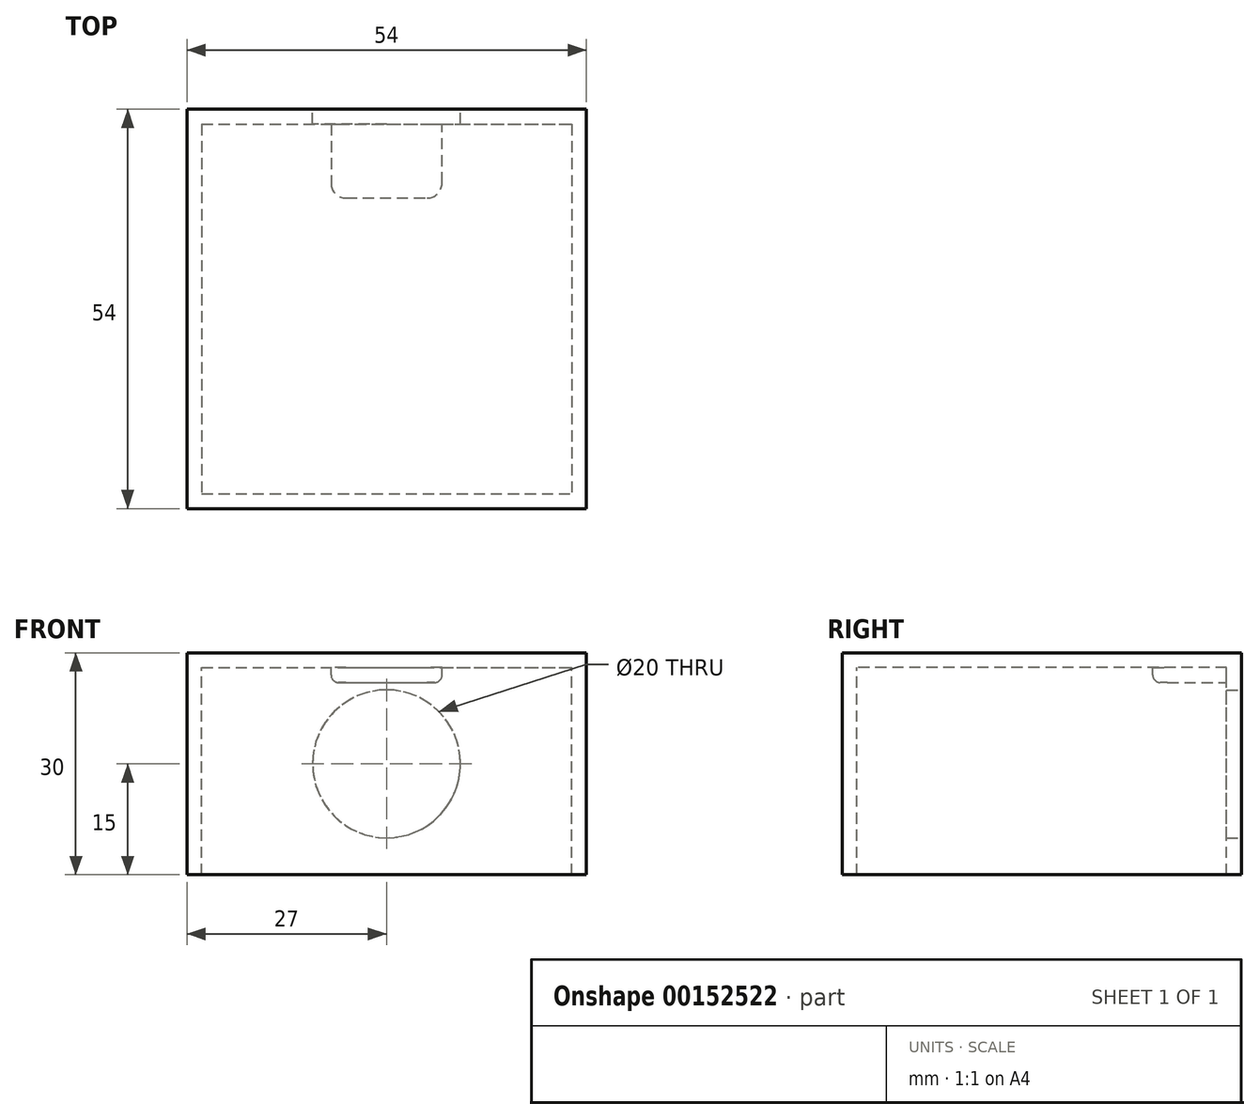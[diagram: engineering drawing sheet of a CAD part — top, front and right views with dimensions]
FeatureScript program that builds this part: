
annotation { "Feature Type Name" : "Feature", "Feature Type Description" : "" }
export const myFeature = defineFeature(function(context is Context, id is Id, definition is map)
    precondition{}
    {
        {
            var Q0;
            Q0=qCreatedBy(makeId("Top.planeOp"),FACE);
            var sketch = newSketch(context, id + "F0", { "sketchPlane" : qUnion([Q0])});
            skLineSegment(sketch, "E0.bottom", {"start": v(-27, 27) * mm, "end": v(27, 27) * mm});
            skLineSegment(sketch, "E0.top", {"start": v(-27, -27) * mm, "end": v(27, -27) * mm});
            skLineSegment(sketch, "E0.left", {"start": v(-27, 27) * mm, "end": v(-27, -27) * mm});
            skLineSegment(sketch, "E0.right", {"start": v(27, 27) * mm, "end": v(27, -27) * mm});
            skPoint(sketch, "E0.middle", {"position": v(0, 0) * mm});
            skLineSegment(sketch, "E1.bottom", {"start": v(-25, 25) * mm, "end": v(25, 25) * mm});
            skLineSegment(sketch, "E1.top", {"start": v(-25, -25) * mm, "end": v(25, -25) * mm});
            skLineSegment(sketch, "E1.left", {"start": v(-25, 25) * mm, "end": v(-25, -25) * mm});
            skLineSegment(sketch, "E1.right", {"start": v(25, 25) * mm, "end": v(25, -25) * mm});
            skSolve(sketch);
        }
        {
            var Q0;
            Q0=makeQuery(id+"F0.imprint","IMPRINT",FACE,{"disambiguationData":[TD([[makeQuery(id+"F0.imprint","IMPRINT",EDGE,{"derivedFrom":sQuery(id+"F0.wireOp",EDGE,"E1.bottom")}),-1.0]])]});
            var Q1;
            Q1=makeQuery(id+"F0.imprint","IMPRINT",FACE,{"disambiguationData":[TD([[makeQuery(id+"F0.imprint","IMPRINT",EDGE,{"derivedFrom":sQuery(id+"F0.wireOp",EDGE,"E0.bottom")}),-1.0]])]});
            extrude(context, id + "F1", {"entities" : qUnion([Q0, Q1]), "oppositeDirection" : true, "depth" : 2 * mm});
        }
        {
            var Q0;
            Q0=makeQuery(id+"F0.imprint","IMPRINT",FACE,{"disambiguationData":[TD([[makeQuery(id+"F0.imprint","IMPRINT",EDGE,{"derivedFrom":sQuery(id+"F0.wireOp",EDGE,"E0.bottom")}),-1.0]])]});
            extrude(context, id + "F2", {"entities" : qUnion([Q0]), "operationType" : NewBodyOperationType.ADD, "oppositeDirection" : true, "depth" : 30 * mm});
        }
        {
            var Q0;
            {var subQ0=sQuery(id+"F0.wireOp",EDGE,"E0.bottom");Q0=makeQuery(id+"F2.boolean.opBoolean","MERGE",FACE,{"derivedFrom":[makeQuery(id+"F1.opExtrude","SWEPT_FACE",FACE,{"disambiguationData":[OSD([subQ0])]}),makeQuery(id+"F2.opExtrude","SWEPT_FACE",FACE,{"disambiguationData":[OSD([subQ0])]})]});}
            var sketch = newSketch(context, id + "F3", { "sketchPlane" : qUnion([Q0])});
            skLineSegment(sketch, "E2.0", {"start": v(27, -30) * mm, "end": v(-27, -30) * mm});
            skLineSegment(sketch, "E3.0", {"start": v(27, 0) * mm, "end": v(-27, 0) * mm});
            skLineSegment(sketch, "E4", {"start": v(27, 0) * mm, "end": v(-27, -30) * mm, "construction": true});
            skCircle(sketch, "E5", {"center": v(0, -15) * mm, "radius": 10 * mm});
            skSolve(sketch);
        }
        {
            var Q0;
            Q0=makeQuery(id+"F3.imprint","IMPRINT",FACE,{"disambiguationData":[TD([[makeQuery(id+"F3.imprint","IMPRINT",EDGE,{"derivedFrom":sQuery(id+"F3.wireOp",EDGE,"E5")}),1.0]])]});
            extrude(context, id + "F4", {"entities" : qUnion([Q0]), "operationType" : NewBodyOperationType.REMOVE, "endBound" : BoundingType.UP_TO_NEXT, "oppositeDirection" : true, "depth" : 25 * mm});
        }
        {
            var Q0;
            Q0=makeQuery(id+"F1.opExtrude","CAP_FACE",FACE,{"disambiguationData":[OSD([sQuery(id+"F0.wireOp",EDGE,"E0.bottom"),sQuery(id+"F0.wireOp",EDGE,"E0.top"),sQuery(id+"F0.wireOp",EDGE,"E0.left"),sQuery(id+"F0.wireOp",EDGE,"E0.right")])],"isStart":false});
            var sketch = newSketch(context, id + "F5", { "sketchPlane" : qUnion([Q0])});
            skLineSegment(sketch, "E6.0", {"start": v(-25, -25) * mm, "end": v(25, -25) * mm});
            skLineSegment(sketch, "E7", {"start": v(0, 0) * mm, "end": v(0, -25) * mm, "construction": true});
            skLineSegment(sketch, "E8", {"start": v(-7.5, -25) * mm, "end": v(-7.5, -17) * mm});
            skLineSegment(sketch, "E9", {"start": v(-5.5, -15) * mm, "end": v(5.5, -15) * mm});
            skLineSegment(sketch, "E10", {"start": v(7.5, -17) * mm, "end": v(7.5, -25) * mm});
            skPoint(sketch, "E11", {"position": v(0, -15) * mm});
            skPoint(sketch, "E12.visualSharp", {"position": v(-7.5, -15) * mm});
            skArc(sketch, "E12.filletArc", {"start": v(-5.5, -15) * mm, "mid": v(-6.91, -15.59) * mm, "end": v(-7.5, -17) * mm});
            skPoint(sketch, "E13.visualSharp", {"position": v(7.5, -15) * mm});
            skArc(sketch, "E13.filletArc", {"start": v(7.5, -17) * mm, "mid": v(6.91, -15.59) * mm, "end": v(5.5, -15) * mm});
            skSolve(sketch);
        }
        {
            var Q0;
            {var subQ1=sQuery(id+"F5.wireOp",EDGE,"E8");Q0=makeQuery(id+"F5.imprint","IMPRINT",FACE,{"disambiguationData":[TD([[makeQuery(id+"F5.imprint","IMPRINT",EDGE,{"derivedFrom":subQ1}),-1.0]])]});}
            extrude(context, id + "F6", {"entities" : qUnion([Q0]), "operationType" : NewBodyOperationType.ADD, "depth" : 2 * mm});
        }
        {
            var Q0;
            Q0=makeQuery(id+"F6.opExtrude","CAP_EDGE",EDGE,{"disambiguationData":[OSD([sQuery(id+"F5.wireOp",EDGE,"E8")])],"isStart":false});
            var Q1;
            Q1=makeQuery(id+"F6.opExtrude","CAP_EDGE",EDGE,{"disambiguationData":[OSD([sQuery(id+"F5.wireOp",EDGE,"E12.filletArc")])],"isStart":false});
            var Q2;
            Q2=makeQuery(id+"F6.opExtrude","CAP_EDGE",EDGE,{"disambiguationData":[OSD([sQuery(id+"F5.wireOp",EDGE,"E9")])],"isStart":false});
            var Q3;
            Q3=makeQuery(id+"F6.opExtrude","CAP_EDGE",EDGE,{"disambiguationData":[OSD([sQuery(id+"F5.wireOp",EDGE,"E13.filletArc")])],"isStart":false});
            var Q4;
            Q4=makeQuery(id+"F6.opExtrude","CAP_EDGE",EDGE,{"disambiguationData":[OSD([sQuery(id+"F5.wireOp",EDGE,"E10")])],"isStart":false});
            fillet(context, id + "F7", {"entities" : qUnion([Q0, Q1, Q2, Q3, Q4]), "radius" : 1 * mm, "tangentPropagation" : true, "allowEdgeOverflow" : false});
        }
    });
